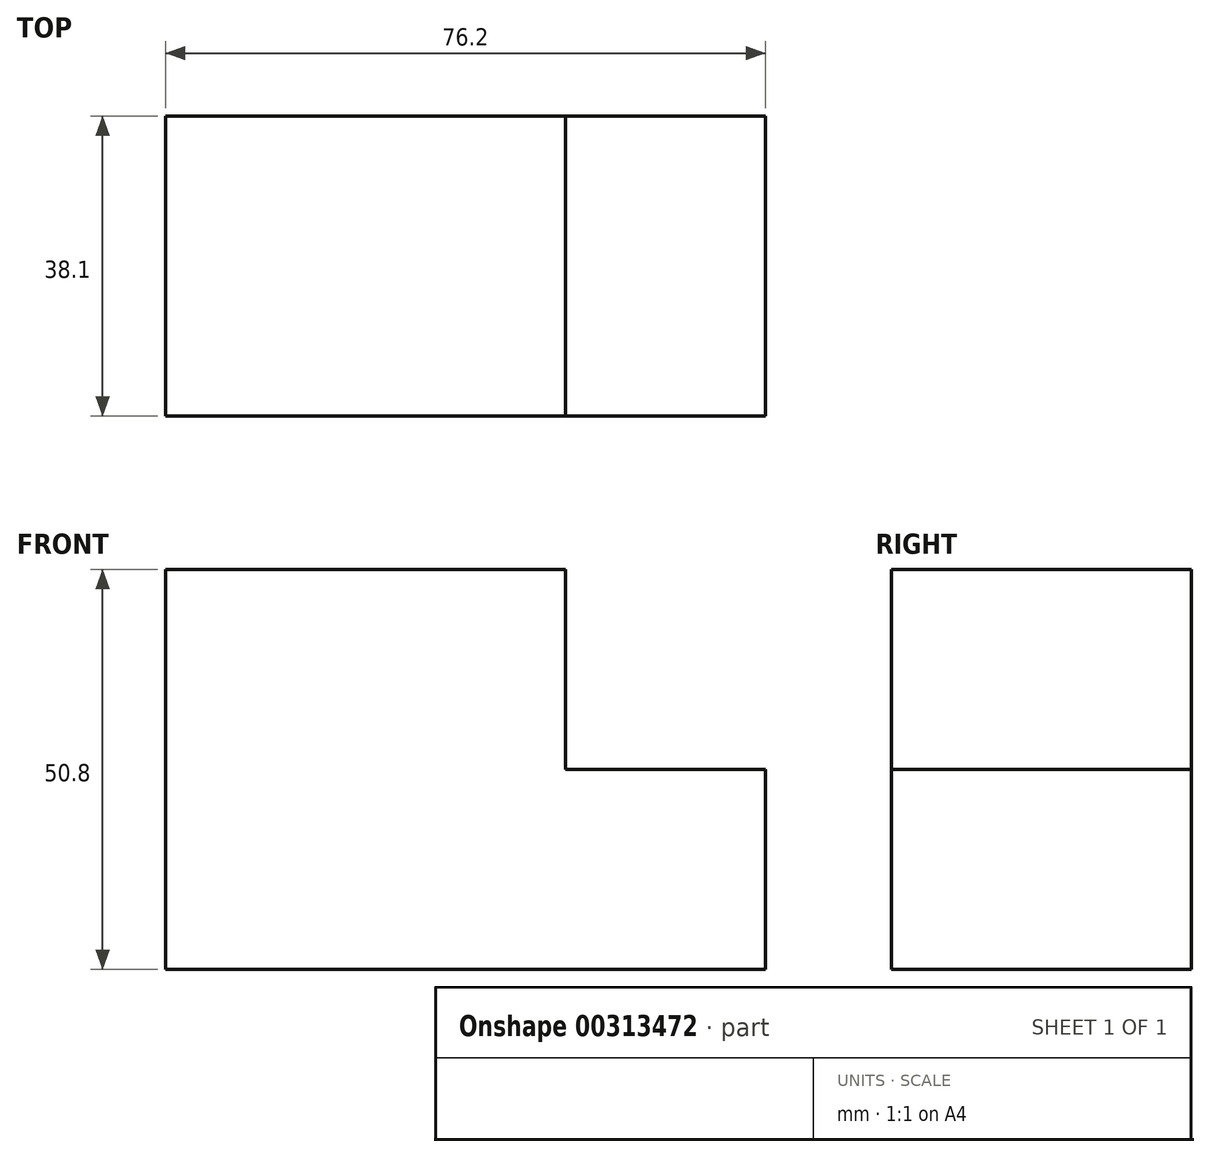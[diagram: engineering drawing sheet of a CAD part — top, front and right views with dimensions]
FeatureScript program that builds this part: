
annotation { "Feature Type Name" : "Feature", "Feature Type Description" : "" }
export const myFeature = defineFeature(function(context is Context, id is Id, definition is map)
    precondition{}
    {
        {
            var Q0;
            Q0=qCreatedBy(makeId("Front.planeOp"),FACE);
            var sketch = newSketch(context, id + "F0", { "sketchPlane" : qUnion([Q0])});
            skLineSegment(sketch, "E0", {"start": v(-30.62, -24.9) * mm, "end": v(45.58, -24.9) * mm});
            skLineSegment(sketch, "E1", {"start": v(45.58, -24.9) * mm, "end": v(45.58, 0.5) * mm});
            skLineSegment(sketch, "E2", {"start": v(45.58, 0.5) * mm, "end": v(20.18, 0.5) * mm});
            skLineSegment(sketch, "E3", {"start": v(20.18, 0.5) * mm, "end": v(20.18, 25.9) * mm});
            skLineSegment(sketch, "E4", {"start": v(20.18, 25.9) * mm, "end": v(-30.62, 25.9) * mm});
            skLineSegment(sketch, "E5", {"start": v(-30.62, 25.9) * mm, "end": v(-30.62, -24.9) * mm});
            skSolve(sketch);
        }
        {
            var Q0;
            Q0=makeQuery(id+"F0.imprint","IMPRINT",FACE,{"disambiguationData":[TD([[makeQuery(id+"F0.imprint","IMPRINT",EDGE,{"derivedFrom":sQuery(id+"F0.wireOp",EDGE,"E0")}),1.0]])]});
            extrude(context, id + "F1", {"entities" : qUnion([Q0]), "depth" : 38.1 * mm});
        }
    });
